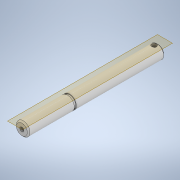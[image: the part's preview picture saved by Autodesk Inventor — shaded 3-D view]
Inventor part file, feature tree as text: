
AUTODESK INVENTOR PART (.ipt)
format: ipt  version: 2022 (Build 260153000, 153)  size: 136,192 bytes
history: native  units: mm
features: sketch x3, extrude x2, revolve x1, plane x1, thread x1
ambient origin geometry x8: Origin, YZ Plane, XZ Plane, XY Plane, X Axis, Y Axis, Z Axis, Center Point
bodies: Solid1 (feature_tree)
feature tree (8):
  revolve  "Revolution1"  [1 undecoded]
  plane  "Work Plane1"
  extrude  "Extrusion1"  Depth=0.5mm
  extrude  "Extrusion2"  Depth=10.0mm
  thread  "Thread1"  [1 undecoded]
  sketch  "Sketch1"  dims[d0=5.0mm d1=100.0mm]
  sketch  "Sketch2"  dims[d2=1.5mm d3=0.5mm]
  sketch  "Sketch3"  dims[d4=135.0deg d5=10.0mm d6=55.0mm d7=1.41mm d8=45.0deg d9=1.414214mm d10=90.0deg d11=3.5mm d12=3.0mm d13=10.0mm d14=0.0mm d15=3.0mm d16=10.0mm d17=0.0mm d18=10.0mm d19=0.0mm]
note: 2 required parameter values undecoded (feature->parameter linkage not recoverable at this tier; creation-order binding heuristic only, values carry confidence <= 0.55)